FCSTD DOCUMENT  (FreeCAD 1.0R39319 (Git))
Label: Week2Sketch1
License: All rights reserved
LicenseURL: https://en.wikipedia.org/wiki/All_rights_reserved
objects: Spreadsheet::Sheet×1, Sketcher::SketchObject×1
note: 2 computed .brp shape members not serialized (recipe doc carries the construction recipe); baked Part::Feature solids carry a one-line shape summary decoded from their .brp

FEATURE [Spreadsheet::Sheet] Spreadsheet
  cells = A1='center_id_cir_dia; B1(center_id_cir_dia)=56; A2='center_od_cir_dia; B2(center_od_cir_dia)=88; A3='top_cir_dia; B3(top_cir_dia)=44; A4='side_cir_dia; B4(side_cir_dia)=36; A5='ydis_center_cir_top; B5(ydis_center_cir_top)=176; A6='ydis_center_bottom; B6(ydis_center_bottom)=120; A7='ydis_side_cir; B7(ydis_side_cir)=38; A8='xdis_side_cir; B8(xdis_side_cir)=96; A9='top_arc_rad; B9(top_arc_rad)=44; A10='bottom_arc_rad; B10(bottom_arc_rad)=32; A11='side_arc_rad; B11(side_arc_rad)=40; A12='slot_angle; B12(slot_angle)=40; A13='slot_rad; B13(slot_rad)=22; A14='slot_outer_rad; B14(slot_outer_rad)=44; A15='diagonal_arc_rad; B15(diagonal_arc_rad)=88; A16='leftcorner_arc_rad; B16(leftcorner_arc_rad)=70
FEATURE [Sketcher::SketchObject] Sketch
  ArcFitTolerance = 1e-06
  FullyConstrained = true
  MakeInternals = false
  expr: Constraints[11] = <<Spreadsheet>>.center_od_cir_dia
  expr: Constraints[12] = <<Spreadsheet>>.center_id_cir_dia
  expr: Constraints[13] = <<Spreadsheet>>.xdis_side_cir
  expr: Constraints[14] = <<Spreadsheet>>.ydis_center_cir_top
  expr: Constraints[15] = <<Spreadsheet>>.ydis_side_cir
  expr: Constraints[16] = <<Spreadsheet>>.top_cir_dia
  expr: Constraints[17] = <<Spreadsheet>>.top_arc_rad
  expr: Constraints[18] = <<Spreadsheet>>.slot_angle
  expr: Constraints[19] = <<Spreadsheet>>.side_cir_dia
  expr: Constraints[25] = <<Spreadsheet>>.slot_outer_rad
  expr: Constraints[26] = <<Spreadsheet>>.ydis_center_bottom
  expr: Constraints[34] = <<Spreadsheet>>.slot_rad
  expr: Constraints[38] = <<Spreadsheet>>.bottom_arc_rad
  expr: Constraints[39] = <<Spreadsheet>>.leftcorner_arc_rad
  expr: Constraints[44] = <<Spreadsheet>>.bottom_arc_rad
  expr: Constraints[45] = <<Spreadsheet>>.side_arc_rad
  expr: Constraints[46] = <<Spreadsheet>>.diagonal_arc_rad
  sketch-geometry (21):
    g0: Circle CenterX=0 CenterY=0 CenterZ=0 NormalX=0 NormalY=0 NormalZ=1 AngleXU=0 Radius=28
    g1: Circle CenterX=0 CenterY=0 CenterZ=0 NormalX=0 NormalY=0 NormalZ=1 AngleXU=0 Radius=44
    g2: LineSegment [constr] StartX=-134.225 StartY=176 StartZ=0 EndX=0 EndY=176 EndZ=0
    g3: LineSegment [constr] StartX=0 StartY=176 StartZ=0 EndX=128.26 EndY=176 EndZ=0
    g4: ArcOfCircle CenterX=0 CenterY=176 CenterZ=0 NormalX=0 NormalY=0 NormalZ=1 AngleXU=0 Radius=44 StartAngle=1e-16 EndAngle=3.14159
    g5: Circle CenterX=96 CenterY=38 CenterZ=0 NormalX=0 NormalY=0 NormalZ=1 AngleXU=0 Radius=18
    g6: Circle CenterX=0 CenterY=176 CenterZ=0 NormalX=0 NormalY=0 NormalZ=1 AngleXU=0 Radius=22
    g7: LineSegment [constr] StartX=0 StartY=0 StartZ=0 EndX=123.534 EndY=-147.222 EndZ=0
    g8: ArcOfCircle CenterX=0 CenterY=-120 CenterZ=0 NormalX=0 NormalY=0 NormalZ=1 AngleXU=0 Radius=44 StartAngle=2.5762 EndAngle=4.96466
    g9: ArcOfCircle CenterX=82.7861 CenterY=-98.6606 CenterZ=0 NormalX=0 NormalY=0 NormalZ=1 AngleXU=0 Radius=44 StartAngle=4.96466 EndAngle=7.3857
    g10: LineSegment StartX=10.9827 StartY=-162.607 StartZ=0 EndX=93.7688 EndY=-141.268 EndZ=0
    g11: ArcOfCircle CenterX=0 CenterY=-120 CenterZ=0 NormalX=0 NormalY=0 NormalZ=1 AngleXU=0 Radius=22 StartAngle=1.82307 EndAngle=4.96466
    g12: ArcOfCircle CenterX=82.7861 CenterY=-98.6606 CenterZ=0 NormalX=0 NormalY=0 NormalZ=1 AngleXU=0 Radius=22 StartAngle=4.96466 EndAngle=8.10626
    g13: LineSegment StartX=-5.49135 StartY=-98.6964 StartZ=0 EndX=77.2947 EndY=-77.3569 EndZ=0
    g14: LineSegment StartX=5.49135 StartY=-141.304 StartZ=0 EndX=88.2774 EndY=-119.964 EndZ=0
    g15: LineSegment StartX=-44 StartY=176 StartZ=0 EndX=-69.2019 EndY=10.5404 EndZ=0
    g16: ArcOfCircle CenterX=0 CenterY=0 CenterZ=0 NormalX=0 NormalY=0 NormalZ=1 AngleXU=0 Radius=70 StartAngle=2.99044 EndAngle=4.03194
    g17: ArcOfCircle CenterX=-64.1728 CenterY=-79.2833 CenterZ=0 NormalX=0 NormalY=0 NormalZ=1 AngleXU=0 Radius=32 StartAngle=5.71779 EndAngle=7.17353
    g18: ArcOfCircle CenterX=117.089 CenterY=-30.8423 CenterZ=0 NormalX=0 NormalY=0 NormalZ=1 AngleXU=0 Radius=32 StartAngle=1.86806 EndAngle=4.24411
    g19: ArcOfCircle CenterX=96 CenterY=38 CenterZ=0 NormalX=0 NormalY=0 NormalZ=1 AngleXU=0 Radius=40 StartAngle=5.00965 EndAngle=7.57908
    g20: ArcOfCircle CenterX=130.745 CenterY=161.194 CenterZ=0 NormalX=0 NormalY=0 NormalZ=1 AngleXU=0 Radius=88 StartAngle=2.97254 EndAngle=4.43749
  constraints (54):
    c: Coincident(g0,g-1)
    c: Coincident(g1,g0)
    c: Horizontal(g2)
    c: PointOnObject(g2,g-2)
    c: Coincident(g3,g2)
    c: Horizontal(g3)
    c: Coincident(g4,g2)
    c: PointOnObject(g4,g2)
    c: PointOnObject(g4,g3)
    c: Coincident(g6,g2)
    c: Coincident(g7,g0)
    c: Diameter(g1) = 88
    c: Diameter(g0) = 56
    c: Distance(g5,g-2) = 96
    c: Distance(g2,g-1) = 176
    c: Distance(g5,g-1) = 38
    c: Diameter(g6) = 44
    c: Radius(g4) = 44
    c: Angle(g-2,g7) = 0.698132
    c: Diameter(g5) = 36
    c: Tangent(g8,g10) = -1.5708
    c: Tangent(g9,g10) = -1.5708
    c: Equal(g8,g9)
    c: PointOnObject(g8,g-2)
    c: PointOnObject(g9,g7)
    c: Radius(g9) = 44
    c: Distance(g8,g-1) = 120
    c: Tangent(g11,g13) = 1.5708
    c: Tangent(g11,g14) = -1.5708
    c: Tangent(g12,g13) = 1.5708
    c: Tangent(g12,g14) = -1.5708
    c: Equal(g11,g12)
    c: Coincident(g11,g8)
    c: Coincident(g12,g9)
    c: Radius(g12) = 22
    c: Coincident(g4,g15)
    c: Tangent(g15,g16) = -1.5708
    c: Tangent(g16,g17) = 1.5708
    c: Radius(g17) = 32
    c: Radius(g16) = 70
    c: Coincident(g16,g0)
    c: Tangent(g18,g19) = 1.5708
    c: Tangent(g19,g20) = 1.5708
    c: Coincident(g20,g4)
    c: Radius(g18) = 32
    c: Radius(g19) = 40
    c: Radius(g20) = 88
    c: Coincident(g19,g5)
    c: Tangent(g8,g17) = 1.5708
    c: Tangent(g9,g18) = 1.5708
    c: Block(g18)
    c: Block(g7)
    c: Block(g2)
    c: Block(g3)
